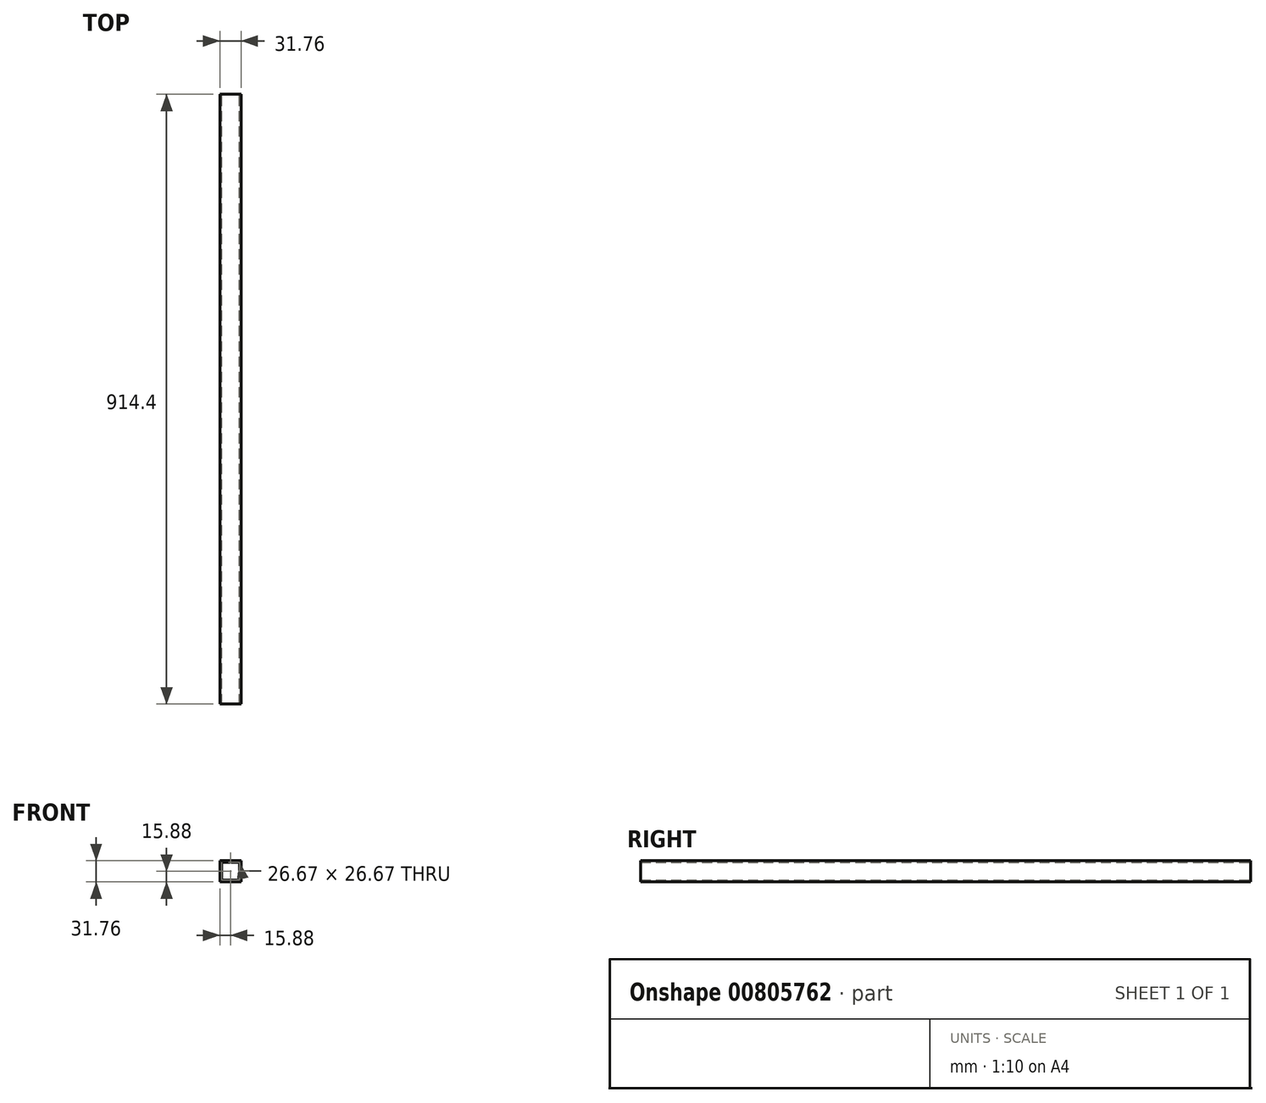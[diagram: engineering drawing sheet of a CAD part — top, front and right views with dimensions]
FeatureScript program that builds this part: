
annotation { "Feature Type Name" : "Feature", "Feature Type Description" : "" }
export const myFeature = defineFeature(function(context is Context, id is Id, definition is map)
    precondition{}
    {
        {
            var Q0;
            Q0=qCreatedBy(makeId("Front.planeOp"),FACE);
            var sketch = newSketch(context, id + "F0", { "sketchPlane" : qUnion([Q0])});
            skLineSegment(sketch, "E0.bottom", {"start": v(15.88, -15.87) * mm, "end": v(-15.87, -15.88) * mm});
            skLineSegment(sketch, "E0.top", {"start": v(15.88, 15.88) * mm, "end": v(-15.87, 15.87) * mm});
            skLineSegment(sketch, "E0.left", {"start": v(15.88, -15.88) * mm, "end": v(15.88, 15.88) * mm});
            skLineSegment(sketch, "E0.right", {"start": v(-15.87, -15.88) * mm, "end": v(-15.87, 15.88) * mm});
            skPoint(sketch, "E0.middle", {"position": v(0, 0) * mm});
            skLineSegment(sketch, "E1.bottom", {"start": v(13.33, -13.33) * mm, "end": v(-13.33, -13.33) * mm});
            skLineSegment(sketch, "E1.top", {"start": v(13.33, 13.33) * mm, "end": v(-13.33, 13.33) * mm});
            skLineSegment(sketch, "E1.left", {"start": v(13.34, -13.33) * mm, "end": v(13.33, 13.33) * mm});
            skLineSegment(sketch, "E1.right", {"start": v(-13.33, -13.33) * mm, "end": v(-13.34, 13.33) * mm});
            skSolve(sketch);
        }
        {
            var Q0;
            Q0=makeQuery(id+"F0.imprint","IMPRINT",FACE,{"disambiguationData":[TD([[makeQuery(id+"F0.imprint","IMPRINT",EDGE,{"derivedFrom":sQuery(id+"F0.wireOp",EDGE,"E0.bottom")}),-1.0]])]});
            extrude(context, id + "F1", {"entities" : qUnion([Q0]), "endBound" : BoundingType.SYMMETRIC, "depth" : 914.4 * mm, "offsetDistance" : 25.4 * mm});
        }
    });
